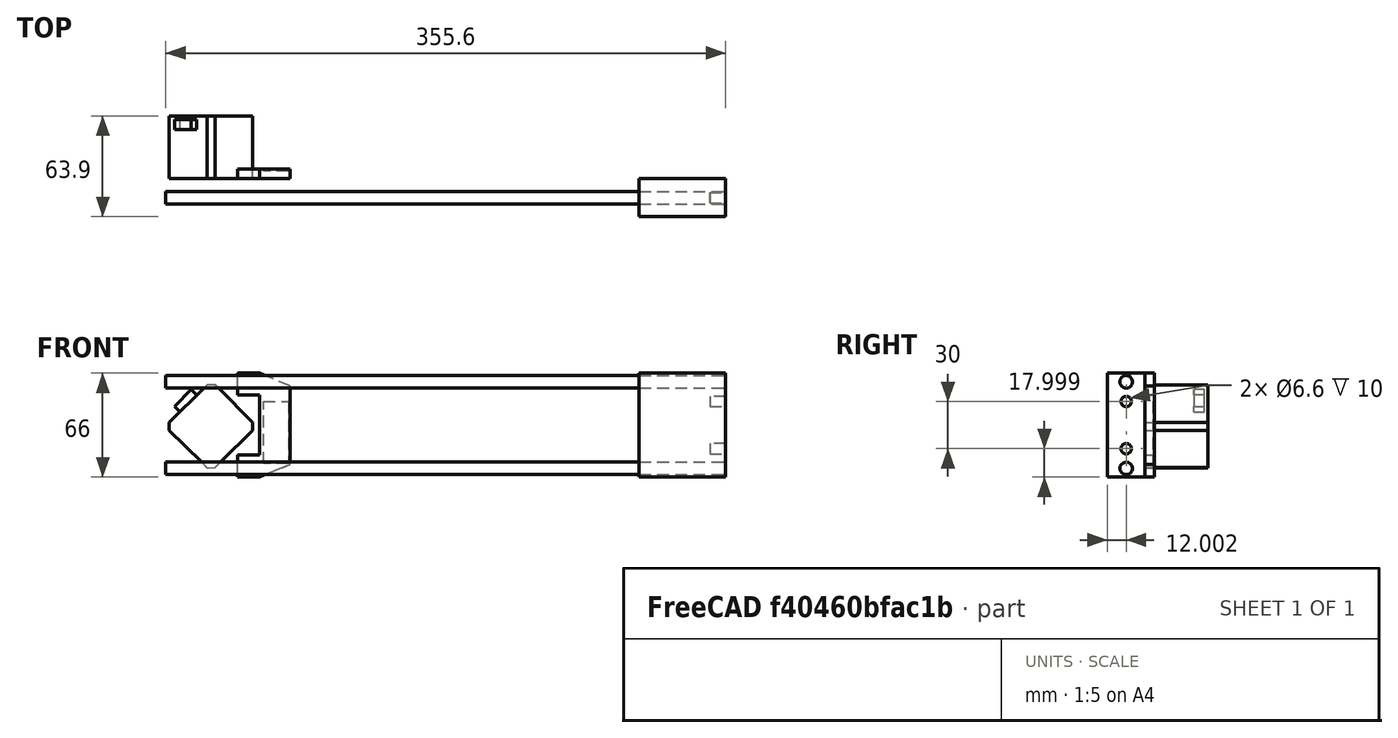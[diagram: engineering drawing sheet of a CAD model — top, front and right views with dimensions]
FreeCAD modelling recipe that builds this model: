
FCSTD DOCUMENT  (FreeCAD 0.16R6705 (Git))
Label: D3D_Circuit_Mill_X_Axis
License: All rights reserved
LicenseURL: http://en.wikipedia.org/wiki/All_rights_reserved
objects: PartDesign::Pocket×3, Part::Cylinder×2, Part::Feature×2, PartDesign::Pad×1, App::DocumentObjectGroup×1
note: 12 computed .brp shape members not serialized (recipe doc carries the construction recipe); baked Part::Feature solids carry a one-line shape summary decoded from their .brp

FEATURE [PartDesign::Pad] Pad001
  Length = 5
  Length2 = 100
  Placement = pos=(4.99156,19.5217,-62.0829) rot=(0.57735,0.57735,0.57735;4.18879rad)
  Type = 0
FEATURE [PartDesign::Pocket] Pocket
  Length = 10
  Placement = pos=(-5.91016,-4.47833,-47.4564) rot=(-1,0,0;1.5708rad)
  Type = 0
FEATURE [Part::Cylinder] Cylinder
  Angle = 360
  Height = 355.6
  Placement = pos=(-23.8449,7.52167,-33.731) rot=(0.57735,-0.57735,0.57735;4.18879rad)
  Radius = 4
FEATURE [Part::Feature] Fusion001  label="D3D End Stop Interface simple001"
  Placement = pos=(8.15515,19.5217,-61.231) rot=(-1,0,0;1.5708rad)
  shape: bbox 33.5 x 6 x 66 mm, 17 faces (baked)
FEATURE [PartDesign::Pocket] Pocket002
  Length = 60
  Placement = pos=(159.909,-4.11958,-66.0258) rot=(-1,0,0;1.5708rad)
  Type = 0
FEATURE [Part::Cylinder] Cylinder001
  Angle = 360
  Height = 355.6
  Placement = pos=(-23.8449,7.52167,-88.731) rot=(0.57735,-0.57735,0.57735;4.18879rad)
  Radius = 4
FEATURE [PartDesign::Pocket] Pocket003
  Length = 100
  Type = 0
FEATURE [Part::Feature] Pocket006
  Placement = pos=(330.208,19.5185,-47.4564) rot=(0,-0.707107,0.707107;3.14159rad)
  shape: bbox 55 x 24 x 66 mm, 10 faces (baked)
FEATURE [App::DocumentObjectGroup] Construction
